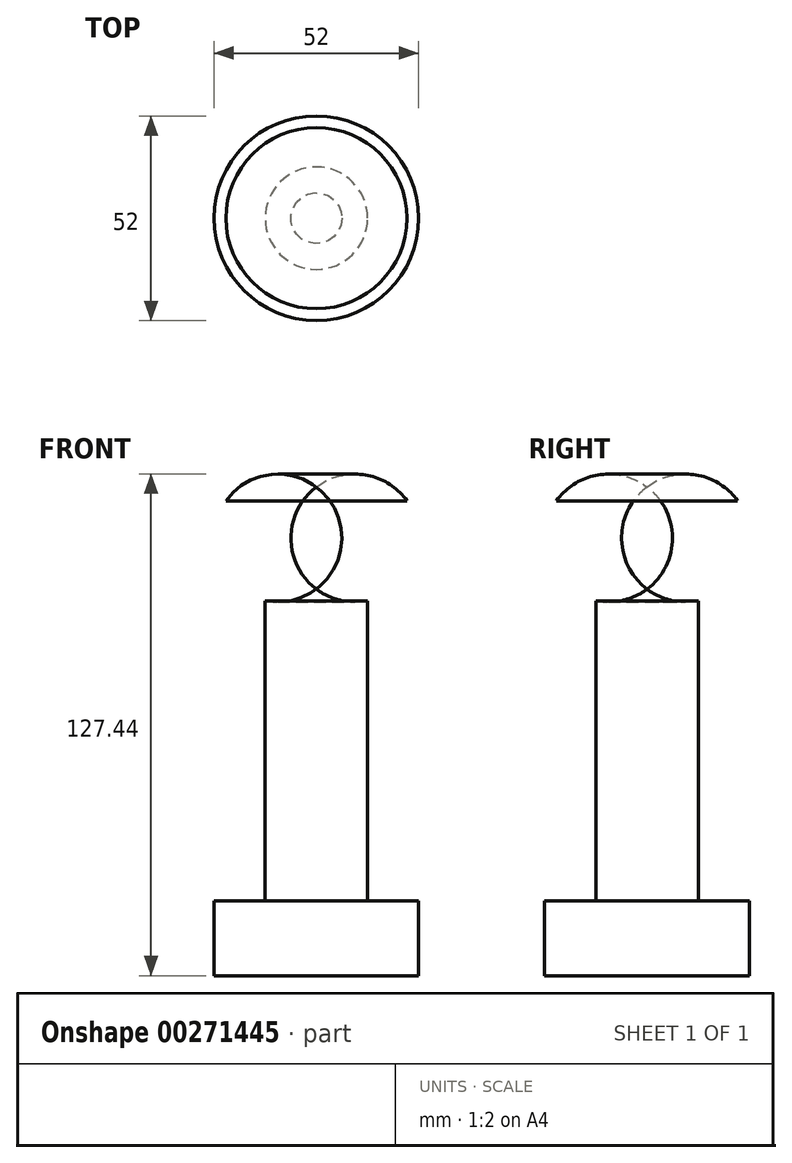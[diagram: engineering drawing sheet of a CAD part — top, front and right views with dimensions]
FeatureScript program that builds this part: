
annotation { "Feature Type Name" : "Feature", "Feature Type Description" : "" }
export const myFeature = defineFeature(function(context is Context, id is Id, definition is map)
    precondition{}
    {
        {
            var Q0;
            Q0=qCreatedBy(makeId("Front.planeOp"),FACE);
            var sketch = newSketch(context, id + "F0", { "sketchPlane" : qUnion([Q0])});
            skLineSegment(sketch, "E0", {"start": v(0, 0) * mm, "end": v(26, 0) * mm});
            skLineSegment(sketch, "E1", {"start": v(26, 0) * mm, "end": v(26, 19.05) * mm});
            skLineSegment(sketch, "E2", {"start": v(26, 19.05) * mm, "end": v(13, 19.05) * mm});
            skLineSegment(sketch, "E3", {"start": v(13, 19.05) * mm, "end": v(13, 95.25) * mm});
            skLineSegment(sketch, "E4", {"start": v(0, 0) * mm, "end": v(0, 120.65) * mm});
            skLineSegment(sketch, "E5", {"start": v(0, 120.65) * mm, "end": v(23, 120.65) * mm});
            skArc(sketch, "E6", {"start": v(13, 95.25) * mm, "mid": v(24.91, 105.23) * mm, "end": v(23, 120.65) * mm});
            skSolve(sketch);
        }
        {
            var Q0;
            Q0=makeQuery(id+"F0.imprint","IMPRINT",FACE,{"disambiguationData":[TD([[makeQuery(id+"F0.imprint","IMPRINT",EDGE,{"derivedFrom":sQuery(id+"F0.wireOp",EDGE,"E0")}),1.0]])]});
            var Q1;
            Q1=sQuery(id+"F0.wireOp",EDGE,"E4");
            revolve(context, id + "F1", {"entities" : qUnion([Q0]), "axis" : qUnion([Q1]), "revolveType" : RevolveType.FULL});
        }
    });
